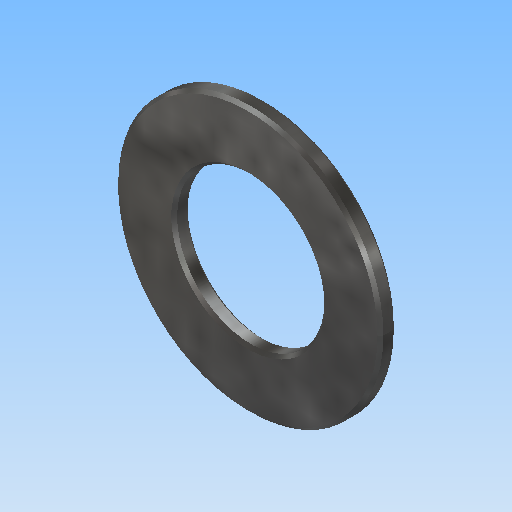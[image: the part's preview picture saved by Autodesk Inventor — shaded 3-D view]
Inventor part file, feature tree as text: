
AUTODESK INVENTOR PART (.ipt)
format: ipt  version: 2018 (Build 220112000, 112)  size: 137,728 bytes
history: native  units: mm
features: extrude x1, chamfer x1, sketch x1
ambient origin geometry x8: Origin, YZ Plane, XZ Plane, XY Plane, X Axis, Y Axis, Z Axis, Center Point
bodies: Solid1 (feature_tree)
feature tree (3):
  extrude  "Extrusion1"  Depth=1.1mm
  chamfer  "Chamfer1"  Distance=1.1mm
  sketch  "Sketch1"  dims[d0=10.0mm d1=18.0mm d2=1.1mm d3=0.0mm d4=0.2mm d5=2.0mm d6=45.0deg]
